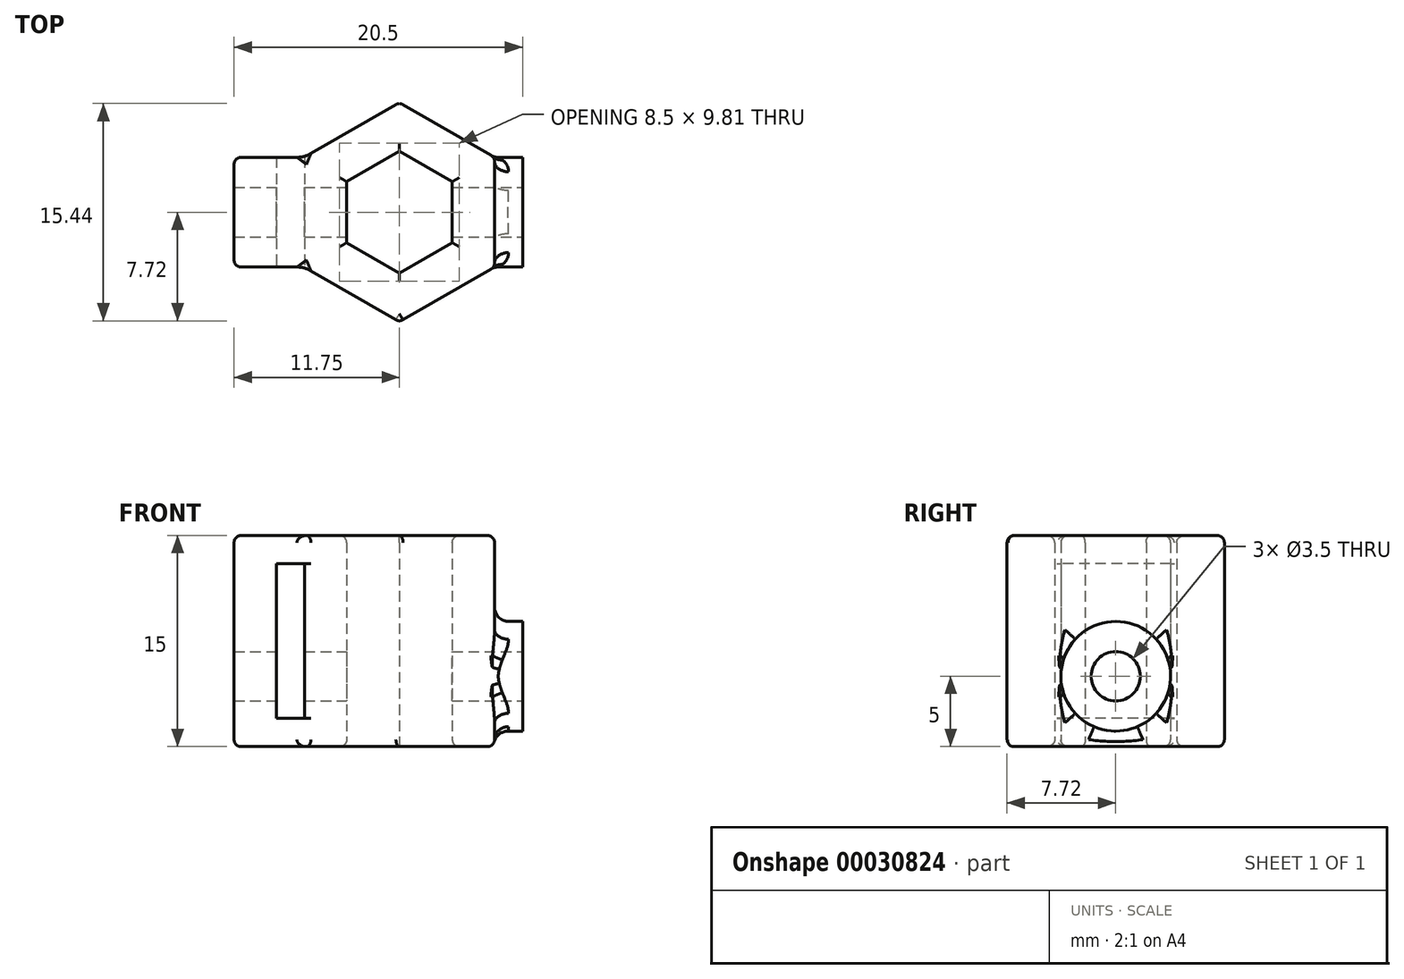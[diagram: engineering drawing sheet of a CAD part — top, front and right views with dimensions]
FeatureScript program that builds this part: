
annotation { "Feature Type Name" : "Feature", "Feature Type Description" : "" }
export const myFeature = defineFeature(function(context is Context, id is Id, definition is map)
    precondition{}
    {
        {
            var Q0;
            Q0=qCreatedBy(makeId("Top.planeOp"),FACE);
            var sketch = newSketch(context, id + "F0", { "sketchPlane" : qUnion([Q0])});
            skCircle(sketch, "E0.cCircle", {"center": v(0, 0) * mm, "radius": 3.75 * mm, "construction": true});
            skLineSegment(sketch, "E0.0", {"start": v(3.75, 2.17) * mm, "end": v(3.75, -2.17) * mm});
            skLineSegment(sketch, "E0.1", {"start": v(3.75, -2.17) * mm, "end": v(0, -4.33) * mm});
            skLineSegment(sketch, "E0.2", {"start": v(0, -4.33) * mm, "end": v(-3.75, -2.17) * mm});
            skLineSegment(sketch, "E0.3", {"start": v(-3.75, -2.17) * mm, "end": v(-3.75, 2.17) * mm});
            skLineSegment(sketch, "E0.4", {"start": v(-3.75, 2.17) * mm, "end": v(0, 4.33) * mm});
            skLineSegment(sketch, "E0.5", {"start": v(0, 4.33) * mm, "end": v(3.75, 2.17) * mm});
            skPoint(sketch, "E0.0.midPoint", {"position": v(3.75, 0) * mm});
            skCircle(sketch, "E1.cCircle", {"center": v(0, 0) * mm, "radius": 6.75 * mm, "construction": true});
            skLineSegment(sketch, "E1.0", {"start": v(6.75, 3.9) * mm, "end": v(6.75, -3.9) * mm});
            skLineSegment(sketch, "E1.1", {"start": v(6.75, -3.9) * mm, "end": v(0, -7.8) * mm});
            skLineSegment(sketch, "E1.2", {"start": v(0, -7.8) * mm, "end": v(-6.75, -3.9) * mm});
            skLineSegment(sketch, "E1.3", {"start": v(-6.75, -3.9) * mm, "end": v(-6.75, 3.9) * mm});
            skLineSegment(sketch, "E1.4", {"start": v(-6.75, 3.9) * mm, "end": v(0, 7.8) * mm});
            skLineSegment(sketch, "E1.5", {"start": v(0, 7.8) * mm, "end": v(6.75, 3.9) * mm});
            skPoint(sketch, "E1.0.midPoint", {"position": v(6.75, 0) * mm});
            skSolve(sketch);
        }
        {
            var Q0;
            Q0=makeQuery(id+"F0.imprint","IMPRINT",FACE,{"disambiguationData":[TD([[makeQuery(id+"F0.imprint","IMPRINT",EDGE,{"derivedFrom":sQuery(id+"F0.wireOp",EDGE,"E0.0")}),1.0]])]});
            extrude(context, id + "F1", {"entities" : qUnion([Q0]), "depth" : 15 * mm});
        }
        {
            var Q0;
            Q0=makeQuery(id+"F1.opExtrude","SWEPT_FACE",FACE,{"disambiguationData":[OSD([sQuery(id+"F0.wireOp",EDGE,"E1.0")])]});
            var sketch = newSketch(context, id + "F2", { "sketchPlane" : qUnion([Q0])});
            skCircle(sketch, "E2", {"center": v(0, 5) * mm, "radius": 3.9 * mm});
            skSolve(sketch);
        }
        {
            var Q0;
            Q0 = qSketchRegion(id + "F2", true);
            extrude(context, id + "F3", {"entities" : qUnion([Q0]), "operationType" : NewBodyOperationType.ADD, "depth" : 2 * mm});
        }
        {
            var Q0;
            Q0=makeQuery(id+"F1.opExtrude","SWEPT_FACE",FACE,{"disambiguationData":[OSD([sQuery(id+"F0.wireOp",EDGE,"E1.3")])]});
            var sketch = newSketch(context, id + "F4", { "sketchPlane" : qUnion([Q0])});
            skLineSegment(sketch, "E3.bottom", {"start": v(-3.9, 15) * mm, "end": v(3.9, 15) * mm});
            skLineSegment(sketch, "E3.top", {"start": v(-3.9, 0) * mm, "end": v(3.9, 0) * mm});
            skLineSegment(sketch, "E3.left", {"start": v(-3.9, 15) * mm, "end": v(-3.9, 0) * mm});
            skLineSegment(sketch, "E3.right", {"start": v(3.9, 15) * mm, "end": v(3.9, 0) * mm});
            skSolve(sketch);
        }
        {
            var Q0;
            Q0 = qSketchRegion(id + "F4", true);
            extrude(context, id + "F5", {"entities" : qUnion([Q0]), "operationType" : NewBodyOperationType.ADD, "depth" : 5 * mm});
        }
        {
            var Q0;
            Q0=makeQuery(id+"F5.opExtrude","SWEPT_FACE",FACE,{"disambiguationData":[OSD([sQuery(id+"F4.wireOp",EDGE,"E3.right")])]});
            var sketch = newSketch(context, id + "F6", { "sketchPlane" : qUnion([Q0])});
            skLineSegment(sketch, "E4.bottom", {"start": v(-6.75, 13) * mm, "end": v(-8.75, 13) * mm});
            skLineSegment(sketch, "E4.top", {"start": v(-6.75, 2) * mm, "end": v(-8.75, 2) * mm});
            skLineSegment(sketch, "E4.left", {"start": v(-6.75, 13) * mm, "end": v(-6.75, 2) * mm});
            skLineSegment(sketch, "E4.right", {"start": v(-8.75, 13) * mm, "end": v(-8.75, 2) * mm});
            skSolve(sketch);
        }
        {
            var Q0;
            Q0 = qSketchRegion(id + "F6", true);
            extrude(context, id + "F7", {"entities" : qUnion([Q0]), "operationType" : NewBodyOperationType.REMOVE, "endBound" : BoundingType.THROUGH_ALL, "oppositeDirection" : true, "depth" : 25 * mm});
        }
        {
            var Q0;
            Q0=makeQuery(id+"F3.opExtrude","CAP_FACE",FACE,{"disambiguationData":[OSD([sQuery(id+"F2.wireOp",EDGE,"E2")])],"isStart":false});
            var sketch = newSketch(context, id + "F8", { "sketchPlane" : qUnion([Q0])});
            skCircle(sketch, "E5", {"center": v(0, 5) * mm, "radius": 1.75 * mm});
            skSolve(sketch);
        }
        {
            var Q0;
            Q0 = qSketchRegion(id + "F8", true);
            extrude(context, id + "F9", {"entities" : qUnion([Q0]), "operationType" : NewBodyOperationType.REMOVE, "endBound" : BoundingType.THROUGH_ALL, "oppositeDirection" : true, "depth" : 25 * mm});
        }
        {
            var Q0;
            Q0=makeQuery(id+"F5.boolean.opBoolean","MERGE",FACE,{"derivedFrom":[makeQuery(id+"F1.opExtrude","CAP_FACE",FACE,{"disambiguationData":[OSD([sQuery(id+"F0.wireOp",EDGE,"E0.0"),sQuery(id+"F0.wireOp",EDGE,"E0.1"),sQuery(id+"F0.wireOp",EDGE,"E0.2"),sQuery(id+"F0.wireOp",EDGE,"E0.3"),sQuery(id+"F0.wireOp",EDGE,"E0.4"),sQuery(id+"F0.wireOp",EDGE,"E0.5"),sQuery(id+"F0.wireOp",EDGE,"E1.0"),sQuery(id+"F0.wireOp",EDGE,"E1.1"),sQuery(id+"F0.wireOp",EDGE,"E1.2"),sQuery(id+"F0.wireOp",EDGE,"E1.3"),sQuery(id+"F0.wireOp",EDGE,"E1.4"),sQuery(id+"F0.wireOp",EDGE,"E1.5")])],"isStart":false}),makeQuery(id+"F5.opExtrude","SWEPT_FACE",FACE,{"disambiguationData":[OSD([sQuery(id+"F4.wireOp",EDGE,"E3.bottom")])]})]});
            var Q1;
            Q1=makeQuery(id+"F5.boolean.opBoolean","MERGE",FACE,{"derivedFrom":[makeQuery(id+"F1.opExtrude","CAP_FACE",FACE,{"disambiguationData":[OSD([sQuery(id+"F0.wireOp",EDGE,"E0.0"),sQuery(id+"F0.wireOp",EDGE,"E0.1"),sQuery(id+"F0.wireOp",EDGE,"E0.2"),sQuery(id+"F0.wireOp",EDGE,"E0.3"),sQuery(id+"F0.wireOp",EDGE,"E0.4"),sQuery(id+"F0.wireOp",EDGE,"E0.5"),sQuery(id+"F0.wireOp",EDGE,"E1.0"),sQuery(id+"F0.wireOp",EDGE,"E1.1"),sQuery(id+"F0.wireOp",EDGE,"E1.2"),sQuery(id+"F0.wireOp",EDGE,"E1.3"),sQuery(id+"F0.wireOp",EDGE,"E1.4"),sQuery(id+"F0.wireOp",EDGE,"E1.5")])],"isStart":true}),makeQuery(id+"F5.opExtrude","SWEPT_FACE",FACE,{"disambiguationData":[OSD([sQuery(id+"F4.wireOp",EDGE,"E3.top")])]})]});
            var Q2;
            Q2=makeQuery(id+"F5.opExtrude","CAP_EDGE",EDGE,{"disambiguationData":[OSD([sQuery(id+"F4.wireOp",EDGE,"E3.right")])],"isStart":false});
            var Q3;
            Q3=makeQuery(id+"F1.opExtrude","SWEPT_EDGE",EDGE,{"disambiguationData":[OSD([sQuery(id+"F0.wireOp",EDGE,"E1.1"),sQuery(id+"F0.wireOp",EDGE,"E1.2")])]});
            var Q4;
            {var subQ0=sQuery(id+"F0.wireOp",EDGE,"E1.0");var subQ1=sQuery(id+"F0.wireOp",EDGE,"E1.5");Q4=makeQuery(id+"F3.boolean.opBoolean","SPLIT",EDGE,{"disambiguationData":[TD([makeQuery(id+"F1.opExtrude","CAP_FACE",FACE,{"disambiguationData":[OSD([sQuery(id+"F0.wireOp",EDGE,"E0.0"),sQuery(id+"F0.wireOp",EDGE,"E0.1"),sQuery(id+"F0.wireOp",EDGE,"E0.2"),sQuery(id+"F0.wireOp",EDGE,"E0.3"),sQuery(id+"F0.wireOp",EDGE,"E0.4"),sQuery(id+"F0.wireOp",EDGE,"E0.5"),subQ0,sQuery(id+"F0.wireOp",EDGE,"E1.1"),sQuery(id+"F0.wireOp",EDGE,"E1.2"),sQuery(id+"F0.wireOp",EDGE,"E1.3"),sQuery(id+"F0.wireOp",EDGE,"E1.4"),subQ1])],"isStart":false})])],"derivedFrom":makeQuery(id+"F1.opExtrude","SWEPT_EDGE",EDGE,{"disambiguationData":[OSD([subQ0,subQ1])]})});}
            var Q5;
            {var subQ0=sQuery(id+"F0.wireOp",EDGE,"E1.0");var subQ1=sQuery(id+"F0.wireOp",EDGE,"E1.1");Q5=makeQuery(id+"F3.boolean.opBoolean","SPLIT",EDGE,{"disambiguationData":[TD([makeQuery(id+"F1.opExtrude","CAP_FACE",FACE,{"disambiguationData":[OSD([sQuery(id+"F0.wireOp",EDGE,"E0.0"),sQuery(id+"F0.wireOp",EDGE,"E0.1"),sQuery(id+"F0.wireOp",EDGE,"E0.2"),sQuery(id+"F0.wireOp",EDGE,"E0.3"),sQuery(id+"F0.wireOp",EDGE,"E0.4"),sQuery(id+"F0.wireOp",EDGE,"E0.5"),subQ0,subQ1,sQuery(id+"F0.wireOp",EDGE,"E1.2"),sQuery(id+"F0.wireOp",EDGE,"E1.3"),sQuery(id+"F0.wireOp",EDGE,"E1.4"),sQuery(id+"F0.wireOp",EDGE,"E1.5")])],"isStart":false})])],"derivedFrom":makeQuery(id+"F1.opExtrude","SWEPT_EDGE",EDGE,{"disambiguationData":[OSD([subQ0,subQ1])]})});}
            var Q6;
            {var subQ0=sQuery(id+"F0.wireOp",EDGE,"E1.0");var subQ1=sQuery(id+"F0.wireOp",EDGE,"E1.5");Q6=makeQuery(id+"F3.boolean.opBoolean","SPLIT",EDGE,{"disambiguationData":[TD([makeQuery(id+"F1.opExtrude","CAP_FACE",FACE,{"disambiguationData":[OSD([sQuery(id+"F0.wireOp",EDGE,"E0.0"),sQuery(id+"F0.wireOp",EDGE,"E0.1"),sQuery(id+"F0.wireOp",EDGE,"E0.2"),sQuery(id+"F0.wireOp",EDGE,"E0.3"),sQuery(id+"F0.wireOp",EDGE,"E0.4"),sQuery(id+"F0.wireOp",EDGE,"E0.5"),subQ0,sQuery(id+"F0.wireOp",EDGE,"E1.1"),sQuery(id+"F0.wireOp",EDGE,"E1.2"),sQuery(id+"F0.wireOp",EDGE,"E1.3"),sQuery(id+"F0.wireOp",EDGE,"E1.4"),subQ1])],"isStart":true})])],"derivedFrom":makeQuery(id+"F1.opExtrude","SWEPT_EDGE",EDGE,{"disambiguationData":[OSD([subQ0,subQ1])]})});}
            var Q7;
            {var subQ0=sQuery(id+"F0.wireOp",EDGE,"E1.0");var subQ1=sQuery(id+"F0.wireOp",EDGE,"E1.1");Q7=makeQuery(id+"F3.boolean.opBoolean","SPLIT",EDGE,{"disambiguationData":[TD([makeQuery(id+"F1.opExtrude","CAP_FACE",FACE,{"disambiguationData":[OSD([sQuery(id+"F0.wireOp",EDGE,"E0.0"),sQuery(id+"F0.wireOp",EDGE,"E0.1"),sQuery(id+"F0.wireOp",EDGE,"E0.2"),sQuery(id+"F0.wireOp",EDGE,"E0.3"),sQuery(id+"F0.wireOp",EDGE,"E0.4"),sQuery(id+"F0.wireOp",EDGE,"E0.5"),subQ0,subQ1,sQuery(id+"F0.wireOp",EDGE,"E1.2"),sQuery(id+"F0.wireOp",EDGE,"E1.3"),sQuery(id+"F0.wireOp",EDGE,"E1.4"),sQuery(id+"F0.wireOp",EDGE,"E1.5")])],"isStart":true})])],"derivedFrom":makeQuery(id+"F1.opExtrude","SWEPT_EDGE",EDGE,{"disambiguationData":[OSD([subQ0,subQ1])]})});}
            fillet(context, id + "F10", {"entities" : qUnion([Q0, Q1, Q2, Q3, Q4, Q5, Q6, Q7]), "radius" : .5 * mm, "tangentPropagation" : true, "allowEdgeOverflow" : false});
        }
        {
            var Q0;
            {var subQ0=sQuery(id+"F0.wireOp",EDGE,"E1.3");var subQ1=sQuery(id+"F0.wireOp",EDGE,"E1.4");var subQ2=sQuery(id+"F4.wireOp",EDGE,"E3.left");Q0=makeQuery(id+"F7.boolean.opBoolean","SPLIT",EDGE,{"disambiguationData":[TD([makeQuery(id+"F1.opExtrude","CAP_FACE",FACE,{"disambiguationData":[OSD([sQuery(id+"F0.wireOp",EDGE,"E0.0"),sQuery(id+"F0.wireOp",EDGE,"E0.1"),sQuery(id+"F0.wireOp",EDGE,"E0.2"),sQuery(id+"F0.wireOp",EDGE,"E0.3"),sQuery(id+"F0.wireOp",EDGE,"E0.4"),sQuery(id+"F0.wireOp",EDGE,"E0.5"),sQuery(id+"F0.wireOp",EDGE,"E1.0"),sQuery(id+"F0.wireOp",EDGE,"E1.1"),sQuery(id+"F0.wireOp",EDGE,"E1.2"),subQ0,subQ1,sQuery(id+"F0.wireOp",EDGE,"E1.5")])],"isStart":false}),makeQuery(id+"F1.opExtrude","SWEPT_FACE",FACE,{"disambiguationData":[OSD([subQ1])]}),makeQuery(id+"F5.opExtrude","SWEPT_FACE",FACE,{"disambiguationData":[OSD([sQuery(id+"F4.wireOp",EDGE,"E3.bottom")])]}),makeQuery(id+"F5.opExtrude","SWEPT_FACE",FACE,{"disambiguationData":[OSD([subQ2])]}),makeQuery(id+"F7.opExtrude","SWEPT_FACE",FACE,{"disambiguationData":[OSD([sQuery(id+"F6.wireOp",EDGE,"E4.bottom")])]}),makeQuery(id+"F7.opExtrude","SWEPT_FACE",FACE,{"disambiguationData":[OSD([sQuery(id+"F6.wireOp",EDGE,"E4.left")])]})])],"derivedFrom":makeQuery(id+"F5.boolean.opBoolean","MERGE",EDGE,{"derivedFrom":[makeQuery(id+"F1.opExtrude","SWEPT_EDGE",EDGE,{"disambiguationData":[OSD([subQ0,subQ1])]}),makeQuery(id+"F5.opExtrude","CAP_EDGE",EDGE,{"disambiguationData":[OSD([subQ2])],"isStart":true})]})});}
            var Q1;
            {var subQ0=sQuery(id+"F0.wireOp",EDGE,"E1.3");var subQ1=sQuery(id+"F0.wireOp",EDGE,"E1.4");var subQ2=sQuery(id+"F4.wireOp",EDGE,"E3.left");Q1=makeQuery(id+"F7.boolean.opBoolean","SPLIT",EDGE,{"disambiguationData":[TD([makeQuery(id+"F1.opExtrude","CAP_FACE",FACE,{"disambiguationData":[OSD([sQuery(id+"F0.wireOp",EDGE,"E0.0"),sQuery(id+"F0.wireOp",EDGE,"E0.1"),sQuery(id+"F0.wireOp",EDGE,"E0.2"),sQuery(id+"F0.wireOp",EDGE,"E0.3"),sQuery(id+"F0.wireOp",EDGE,"E0.4"),sQuery(id+"F0.wireOp",EDGE,"E0.5"),sQuery(id+"F0.wireOp",EDGE,"E1.0"),sQuery(id+"F0.wireOp",EDGE,"E1.1"),sQuery(id+"F0.wireOp",EDGE,"E1.2"),subQ0,subQ1,sQuery(id+"F0.wireOp",EDGE,"E1.5")])],"isStart":true}),makeQuery(id+"F1.opExtrude","SWEPT_FACE",FACE,{"disambiguationData":[OSD([subQ1])]}),makeQuery(id+"F5.opExtrude","SWEPT_FACE",FACE,{"disambiguationData":[OSD([sQuery(id+"F4.wireOp",EDGE,"E3.top")])]}),makeQuery(id+"F5.opExtrude","SWEPT_FACE",FACE,{"disambiguationData":[OSD([subQ2])]}),makeQuery(id+"F7.opExtrude","SWEPT_FACE",FACE,{"disambiguationData":[OSD([sQuery(id+"F6.wireOp",EDGE,"E4.top")])]}),makeQuery(id+"F7.opExtrude","SWEPT_FACE",FACE,{"disambiguationData":[OSD([sQuery(id+"F6.wireOp",EDGE,"E4.left")])]})])],"derivedFrom":makeQuery(id+"F5.boolean.opBoolean","MERGE",EDGE,{"derivedFrom":[makeQuery(id+"F1.opExtrude","SWEPT_EDGE",EDGE,{"disambiguationData":[OSD([subQ0,subQ1])]}),makeQuery(id+"F5.opExtrude","CAP_EDGE",EDGE,{"disambiguationData":[OSD([subQ2])],"isStart":true})]})});}
            var Q2;
            {var subQ0=sQuery(id+"F0.wireOp",EDGE,"E1.2");var subQ1=sQuery(id+"F0.wireOp",EDGE,"E1.3");var subQ2=sQuery(id+"F4.wireOp",EDGE,"E3.right");Q2=makeQuery(id+"F7.boolean.opBoolean","SPLIT",EDGE,{"disambiguationData":[TD([makeQuery(id+"F5.opExtrude","SWEPT_FACE",FACE,{"disambiguationData":[OSD([sQuery(id+"F4.wireOp",EDGE,"E3.bottom")])]})])],"derivedFrom":makeQuery(id+"F5.boolean.opBoolean","MERGE",EDGE,{"derivedFrom":[makeQuery(id+"F1.opExtrude","SWEPT_EDGE",EDGE,{"disambiguationData":[OSD([subQ0,subQ1])]}),makeQuery(id+"F5.opExtrude","CAP_EDGE",EDGE,{"disambiguationData":[OSD([subQ2])],"isStart":true})]})});}
            var Q3;
            {var subQ0=sQuery(id+"F0.wireOp",EDGE,"E1.2");var subQ1=sQuery(id+"F0.wireOp",EDGE,"E1.3");var subQ2=sQuery(id+"F4.wireOp",EDGE,"E3.right");Q3=makeQuery(id+"F7.boolean.opBoolean","SPLIT",EDGE,{"disambiguationData":[TD([makeQuery(id+"F5.opExtrude","SWEPT_FACE",FACE,{"disambiguationData":[OSD([sQuery(id+"F4.wireOp",EDGE,"E3.top")])]})])],"derivedFrom":makeQuery(id+"F5.boolean.opBoolean","MERGE",EDGE,{"derivedFrom":[makeQuery(id+"F1.opExtrude","SWEPT_EDGE",EDGE,{"disambiguationData":[OSD([subQ0,subQ1])]}),makeQuery(id+"F5.opExtrude","CAP_EDGE",EDGE,{"disambiguationData":[OSD([subQ2])],"isStart":true})]})});}
            fillet(context, id + "F11", {"entities" : qUnion([Q0, Q1, Q2, Q3]), "radius" : 2 * mm, "tangentPropagation" : true, "allowEdgeOverflow" : false});
        }
        {
            var Q0;
            Q0=makeQuery(id+"F3.boolean.opBoolean","SPLIT",EDGE,{"disambiguationData":[OD(1.0)],"derivedFrom":makeQuery(id+"F3.opExtrude","CAP_EDGE",EDGE,{"disambiguationData":[OSD([sQuery(id+"F2.wireOp",EDGE,"E2")])],"isStart":true})});
            fillet(context, id + "F12", {"entities" : qUnion([Q0]), "radius" : 1 * mm, "tangentPropagation" : true, "allowEdgeOverflow" : false});
        }
        {
            var Q0;
            Q0=makeQuery(id+"F5.opExtrude","CAP_EDGE",EDGE,{"disambiguationData":[OSD([sQuery(id+"F4.wireOp",EDGE,"E3.left")])],"isStart":false});
            var Q1;
            Q1=makeQuery(id+"F1.opExtrude","SWEPT_EDGE",EDGE,{"disambiguationData":[OSD([sQuery(id+"F0.wireOp",EDGE,"E1.4"),sQuery(id+"F0.wireOp",EDGE,"E1.5")])]});
            fillet(context, id + "F13", {"entities" : qUnion([Q0, Q1]), "radius" : .5 * mm, "tangentPropagation" : true, "allowEdgeOverflow" : false});
        }
    });
